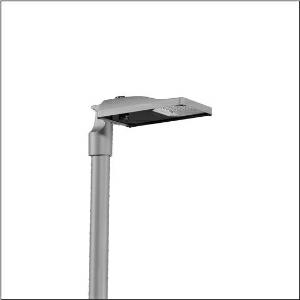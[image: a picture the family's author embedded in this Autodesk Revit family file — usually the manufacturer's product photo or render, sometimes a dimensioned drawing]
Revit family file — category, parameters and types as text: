
# Revit family: streetlight_sl_31_micro___pl52_5xh5h31t08ca_bf49
name_source: partatom
category: Lighting Fixtures
units: mm (PartAtom-declared; Revit-internal decimal feet)

## family parameters
Cut with Voids When Loaded = No
Host = Face
Light Source = No
Part Type = Normal
Room Calculation Point = No
Round Connector Dimension = Use Diameter
Shared = No

## types (1)
- --- (1 x LED, 1420 lm, 10.2 W, 3000K)
    Apparent Load = 10 VA
    CIE Flux Codes = 27 59 98 100 100
    Color Rendering = 70
    Color Temperature = 3000K
    Default Elevation = 1800 mm
    Description = Streetlight SL 31 micro D4i, Desk-Remote mast luminaire for post-top, side-entry; light control with lens of PMMA; light distribution: PL52, direct asymmetric distribution, for standard-compliant lighting for roads and squares; LED: luminous flux: 1.420lm, light colour: 730, colour temperature: 3000K; luminous efficacy: 139,2lm/W; control: pre-setting: logarithmic dimming characteristic, flexible luminous flux parameterisation, time-dependent luminous flux control, constant luminous flux control, power reduction, intelligent temperature release in ECG and LED module, overheat protection; luminaire housing, of diecast aluminium, Siteco® metallic grey (DB 702S), corrosivity category C5 high according to DIN EN ISO 12944; cover of toughened safety glass, transparent, opened without tools; mast flange of diecast aluminium, Siteco® metallic grey (DB 702S), spigot size: 76/60mm, mast flange included unmounted; with cable H07RN-F 2x 1.5mm², cable length: 5,5m, connection cable pre-assembled; mains connection: 220..240V, AC, 50/60Hz; power consumption (at start of service life): 10,2W / (at end of service life): 10,5W / (with reduced operation 50%): 5,3W; protection rating (complete): IP66; insulation class (complete): insulation class II (safety insulation); impact resistance: IK09; certification: CE, ENEC, ENEC+, VDE, UKCA, ZD4i; permissible operating ambient temperature for outdoor applications: -40..+50°C; packaging unit: 1 piece

Light Distribution: PL52
    Height = 76 mm
    Lamp = 1 x LED
    Lamp Light Flux = 1420 lm
    Lamp Power = 10.2 W
    Lamp count = 1
    Length = 467 mm
    Luminous efficacy = 139 lm/W
    Manufacturer = Siteco
    ModVariant = No
    Model = 5XH5H31T08CA
    Number of Poles = 1
    OnlyDefault = Yes
    Power Factor = 1
    Product Name = Streetlight SL 31 micro | PL52
    Product group = mast luminaire | pylon top
    ProductGroupID = 6100
    Protection Class = Protection class II
    Protection Degree = IP 66
    RLX_Detail_Level = 1
    RLX_Emergency_Light_Flux = 0 lm
    RLX_Emergency_Type = 0
    RLX_Emergency_Type_DB = No
    RlxData = <blob elided: 53805 chars, md5=7e256d72>
    Socket = socket
    Standby Power = 0 W
    System Light Flux = 1420 lm
    System Power = 10 W
    Type Comments = factory setting: luminous flux: 100 % | dim-lin: 254 | 386 mA
    Type Image = l_1300315.jpg
    URL = http://relux.com
    VarID = @adj_069067
    Voltage = 0 V
    Weight = 0.00 kg
    Width = 265 mm

## geometry (parser evidence)
native form markers: Blend x4, Sweep x10
no freeform markers — native parametric forms only
